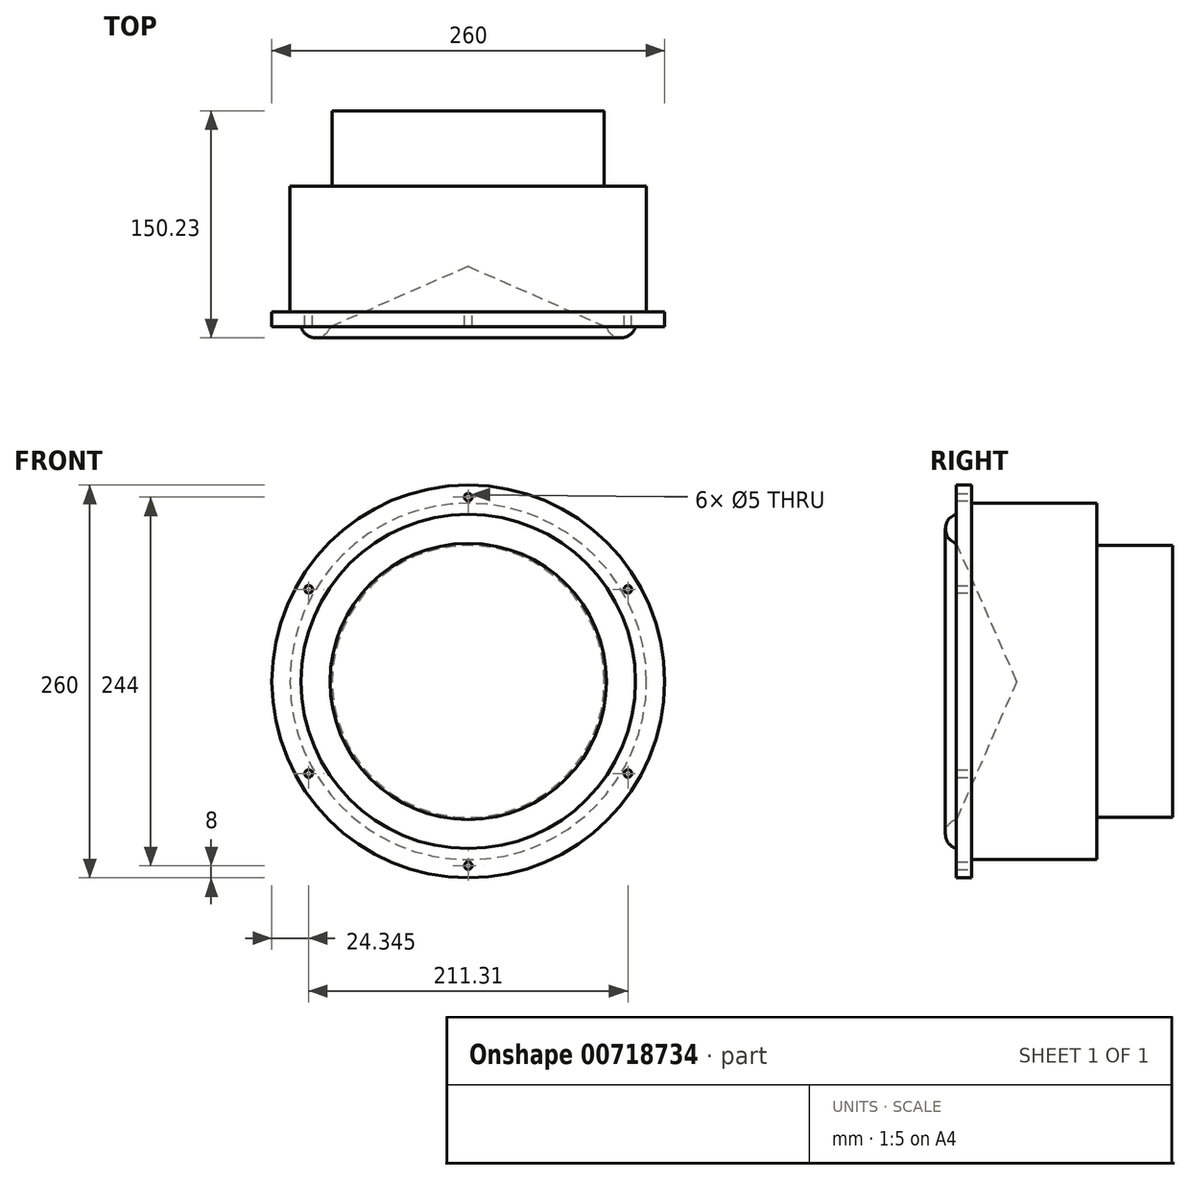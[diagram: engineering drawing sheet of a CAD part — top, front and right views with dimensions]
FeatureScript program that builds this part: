
annotation { "Feature Type Name" : "Feature", "Feature Type Description" : "" }
export const myFeature = defineFeature(function(context is Context, id is Id, definition is map)
    precondition{}
    {
        {
            var Q0;
            Q0=qCreatedBy(makeId("Front.planeOp"),FACE);
            var sketch = newSketch(context, id + "F0", { "sketchPlane" : qUnion([Q0])});
            skCircle(sketch, "E0", {"center": v(0, 0) * mm, "radius": 130 * mm});
            skSolve(sketch);
        }
        {
            var Q0;
            Q0=makeQuery(id+"F0.imprint","IMPRINT",FACE,{"disambiguationData":[TD([[makeQuery(id+"F0.imprint","IMPRINT",EDGE,{"derivedFrom":sQuery(id+"F0.wireOp",EDGE,"E0")}),1.0]])]});
            extrude(context, id + "F1", {"entities" : qUnion([Q0]), "depth" : 10 * mm, "offsetDistance" : 25 * mm});
        }
        {
            var Q0;
            Q0=makeQuery(id+"F1.opExtrude","CAP_FACE",FACE,{"disambiguationData":[OSD([sQuery(id+"F0.wireOp",EDGE,"E0")])],"isStart":true});
            var sketch = newSketch(context, id + "F2", { "sketchPlane" : qUnion([Q0])});
            skCircle(sketch, "E1", {"center": v(0, 0) * mm, "radius": 118 * mm});
            skSolve(sketch);
        }
        {
            var Q0;
            Q0=makeQuery(id+"F2.imprint","IMPRINT",FACE,{"disambiguationData":[TD([[makeQuery(id+"F2.imprint","IMPRINT",EDGE,{"derivedFrom":sQuery(id+"F2.wireOp",EDGE,"E1")}),1.0]])]});
            extrude(context, id + "F3", {"entities" : qUnion([Q0]), "operationType" : NewBodyOperationType.ADD, "depth" : 133 * mm, "offsetDistance" : 25 * mm});
        }
        {
            var Q0;
            Q0=qCreatedBy(makeId("Top.planeOp"),FACE);
            var sketch = newSketch(context, id + "F4", { "sketchPlane" : qUnion([Q0])});
            skLineSegment(sketch, "E2", {"start": v(0, -40) * mm, "end": v(0, 0) * mm});
            skLineSegment(sketch, "E3", {"start": v(0, 0) * mm, "end": v(0, 30) * mm});
            skLineSegment(sketch, "E4", {"start": v(0, 30) * mm, "end": v(160, -40) * mm});
            skLineSegment(sketch, "E5", {"start": v(0, -40) * mm, "end": v(160, -40) * mm});
            skSolve(sketch);
        }
        {
            var Q0;
            Q0=makeQuery(id+"F4.imprint","IMPRINT",FACE,{"disambiguationData":[TD([[makeQuery(id+"F4.imprint","IMPRINT",EDGE,{"derivedFrom":sQuery(id+"F4.wireOp",EDGE,"E2")}),-1.0]])]});
            var Q1;
            Q1=sQuery(id+"F4.wireOp",EDGE,"E2");
            revolve(context, id + "F5", {"operationType" : NewBodyOperationType.REMOVE, "surfaceOperationType" : NewSurfaceOperationType.NEW, "entities" : qUnion([Q0]), "axis" : qUnion([Q1]), "revolveType" : RevolveType.FULL, "oppositeDirection" : true});
        }
        {
            var Q0;
            Q0=qCreatedBy(makeId("Top.planeOp"),FACE);
            var sketch = newSketch(context, id + "F6", { "sketchPlane" : qUnion([Q0])});
            skArc(sketch, "E6", {"start": v(-110.65, -10) * mm, "mid": v(-101.04, -17.23) * mm, "end": v(-91.43, -10) * mm});
            skLineSegment(sketch, "E7", {"start": v(-110.65, -10) * mm, "end": v(-91.43, -10) * mm});
            skSolve(sketch);
        }
        {
            var Q0;
            Q0=makeQuery(id+"F6.imprint","IMPRINT",FACE,{"disambiguationData":[TD([[makeQuery(id+"F6.imprint","IMPRINT",EDGE,{"derivedFrom":sQuery(id+"F6.wireOp",EDGE,"E6")}),1.0]])]});
            var Q1;
            Q1=makeQuery(id+"F5.boolean.opBoolean","INTERSECT",EDGE,{"derivedFrom":[makeQuery(id+"F1.opExtrude","CAP_FACE",FACE,{"disambiguationData":[OSD([sQuery(id+"F0.wireOp",EDGE,"E0")])],"isStart":false}),makeQuery(id+"F5.opRevolve","SWEPT_FACE",FACE,{"disambiguationData":[OSD([sQuery(id+"F4.wireOp",EDGE,"E4")])]})]});
            revolve(context, id + "F7", {"operationType" : NewBodyOperationType.ADD, "surfaceOperationType" : NewSurfaceOperationType.NEW, "entities" : qUnion([Q0]), "axis" : qUnion([Q1]), "revolveType" : RevolveType.FULL});
        }
        {
            var Q0;
            Q0=makeQuery(id+"F1.opExtrude","CAP_FACE",FACE,{"disambiguationData":[OSD([sQuery(id+"F0.wireOp",EDGE,"E0")])],"isStart":true});
            var sketch = newSketch(context, id + "F8", { "sketchPlane" : qUnion([Q0])});
            skPoint(sketch, "E8.0", {"position": v(0, 0) * mm});
            skCircle(sketch, "E9.cCircle", {"center": v(0, 0) * mm, "radius": 122 * mm, "construction": true});
            skLineSegment(sketch, "E9.0", {"start": v(0, 122) * mm, "end": v(105.66, 61) * mm});
            skLineSegment(sketch, "E9.1", {"start": v(105.66, 61) * mm, "end": v(105.66, -61) * mm});
            skLineSegment(sketch, "E9.2", {"start": v(105.66, -61) * mm, "end": v(0, -122) * mm});
            skLineSegment(sketch, "E9.3", {"start": v(0, -122) * mm, "end": v(-105.66, -61) * mm});
            skLineSegment(sketch, "E9.4", {"start": v(-105.66, -61) * mm, "end": v(-105.66, 61) * mm});
            skLineSegment(sketch, "E9.5", {"start": v(-105.66, 61) * mm, "end": v(0, 122) * mm});
            skSolve(sketch);
        }
        {
            var Q0;
            Q0=sQuery(id+"F8.wireOp",VERTEX,"E9.1.start");
            var Q1;
            Q1=sQuery(id+"F8.wireOp",VERTEX,"E9.1.end");
            var Q2;
            Q2=sQuery(id+"F8.wireOp",VERTEX,"E9.3.start");
            var Q3;
            Q3=sQuery(id+"F8.wireOp",VERTEX,"E9.0.start");
            var Q4;
            Q4=sQuery(id+"F8.wireOp",VERTEX,"E9.5.start");
            var Q5;
            Q5=sQuery(id+"F8.wireOp",VERTEX,"E9.4.start");
            var Q6;
            Q6=makeQuery(id+"F1.opExtrude","SWEPT_BODY",BODY,{"disambiguationData":[OSD([sQuery(id+"F0.wireOp",EDGE,"E0")])]});
            hole(context, id + "F9", {"style" : HoleStyle.SIMPLE, "endStyle" : HoleEndStyle.THROUGH, "holeDiameter" : 5 * mm, "majorDiameter" : 5 * mm, "isTappedThrough" : true, "tappedDepth" : 12 * mm, "tapClearance" : 3, "locations" : qUnion([Q0, Q1, Q2, Q3, Q4, Q5]), "scope" : qUnion([Q6])});
        }
        {
            var Q0;
            Q0=makeQuery(id+"F3.opExtrude","CAP_FACE",FACE,{"disambiguationData":[OSD([sQuery(id+"F2.wireOp",EDGE,"E1")])],"isStart":false});
            var sketch = newSketch(context, id + "F10", { "sketchPlane" : qUnion([Q0])});
            skCircle(sketch, "E10", {"center": v(0, 0) * mm, "radius": 90 * mm});
            skSolve(sketch);
        }
        {
            var Q0;
            Q0=makeQuery(id+"F10.imprint","IMPRINT",FACE,{"disambiguationData":[TD([[makeQuery(id+"F10.imprint","IMPRINT",EDGE,{"derivedFrom":sQuery(id+"F10.wireOp",EDGE,"E10")}),-1.0]])]});
            extrude(context, id + "F11", {"entities" : qUnion([Q0]), "operationType" : NewBodyOperationType.REMOVE, "oppositeDirection" : true, "depth" : 50 * mm, "offsetDistance" : 25 * mm});
        }
    });
